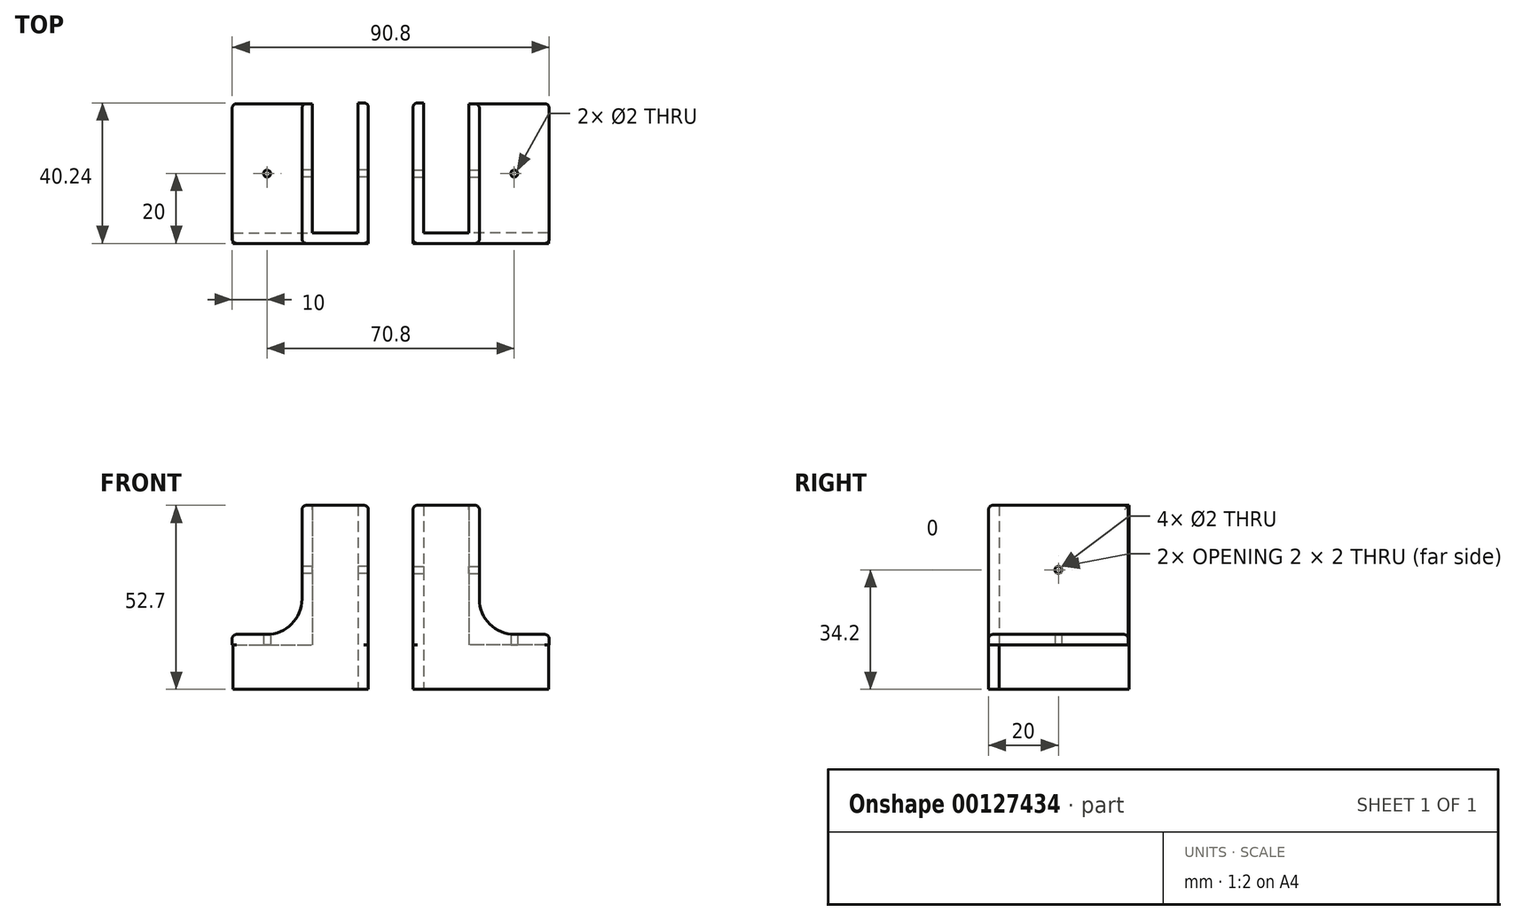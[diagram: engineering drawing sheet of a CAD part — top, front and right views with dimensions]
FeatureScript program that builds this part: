
annotation { "Feature Type Name" : "Feature", "Feature Type Description" : "" }
export const myFeature = defineFeature(function(context is Context, id is Id, definition is map)
    precondition{}
    {
        {
            var Q0;
            Q0=qCreatedBy(makeId("Top.planeOp"),FACE);
            var sketch = newSketch(context, id + "F0", { "sketchPlane" : qUnion([Q0])});
            skLineSegment(sketch, "E0.bottom", {"start": v(0, 0) * mm, "end": v(-20, 0) * mm});
            skLineSegment(sketch, "E0.top", {"start": v(0, 40) * mm, "end": v(-20, 40) * mm});
            skLineSegment(sketch, "E0.left", {"start": v(0, 0) * mm, "end": v(0, 40) * mm});
            skLineSegment(sketch, "E0.right", {"start": v(-20, 0) * mm, "end": v(-20, 40) * mm});
            skLineSegment(sketch, "E1", {"start": v(0, 40) * mm, "end": v(3, 40) * mm});
            skLineSegment(sketch, "E2", {"start": v(3, 40) * mm, "end": v(3, 3) * mm});
            skLineSegment(sketch, "E3", {"start": v(3, 3) * mm, "end": v(16, 3) * mm});
            skLineSegment(sketch, "E4", {"start": v(16, 3) * mm, "end": v(16, 40.24) * mm});
            skLineSegment(sketch, "E5", {"start": v(16, 40.24) * mm, "end": v(19, 40.24) * mm});
            skLineSegment(sketch, "E6", {"start": v(19, 40.24) * mm, "end": v(19, 0) * mm});
            skLineSegment(sketch, "E7", {"start": v(19, 0) * mm, "end": v(0, 0) * mm});
            skLineSegment(sketch, "E8", {"start": v(0, 20) * mm, "end": v(54.2, 20) * mm, "construction": true});
            skLineSegment(sketch, "E9", {"start": v(54.2, 20) * mm, "end": v(-70.8, 20) * mm, "construction": true});
            skCircle(sketch, "E10", {"center": v(-10, 20) * mm, "radius": 1 * mm});
            skPoint(sketch, "E10.centerSnap0", {"position": v(-10, 40) * mm});
            skPoint(sketch, "E10.centerSnap1", {"position": v(-8.3, 20) * mm});
            skLineSegment(sketch, "E11", {"start": v(3, 3) * mm, "end": v(3, 0) * mm});
            skSolve(sketch);
        }
        {
            var Q0;
            Q0=makeQuery(id+"F0.imprint","IMPRINT",FACE,{"disambiguationData":[TD([[makeQuery(id+"F0.imprint","IMPRINT",EDGE,{"derivedFrom":sQuery(id+"F0.wireOp",EDGE,"E0.left")}),-1.0]])]});
            var Q1;
            Q1=makeQuery(id+"F0.imprint","IMPRINT",FACE,{"disambiguationData":[TD([[makeQuery(id+"F0.imprint","IMPRINT",EDGE,{"derivedFrom":sQuery(id+"F0.wireOp",EDGE,"E3")}),-1.0]])]});
            extrude(context, id + "F1", {"entities" : qUnion([Q0, Q1]), "depth" : 40 * mm});
        }
        {
            var Q0;
            Q0 = qSketchRegion(id + "F0", true);
            extrude(context, id + "F2", {"entities" : qUnion([Q0]), "operationType" : NewBodyOperationType.ADD, "depth" : 3 * mm});
        }
        {
            var Q0;
            Q0=makeQuery(id+"F1.opExtrude","SWEPT_FACE",FACE,{"disambiguationData":[OSD([sQuery(id+"F0.wireOp",EDGE,"E0.left")])]});
            var sketch = newSketch(context, id + "F3", { "sketchPlane" : qUnion([Q0])});
            skCircle(sketch, "E12", {"center": v(-20, 21.5) * mm, "radius": 1 * mm});
            skPoint(sketch, "E12.centerSnap0", {"position": v(-20, 40) * mm});
            skPoint(sketch, "E12.centerSnap1", {"position": v(0, 21.5) * mm});
            skSolve(sketch);
        }
        {
            var Q0;
            Q0=makeQuery(id+"F3.imprint","IMPRINT",FACE,{"disambiguationData":[TD([[makeQuery(id+"F3.imprint","IMPRINT",EDGE,{"derivedFrom":sQuery(id+"F3.wireOp",EDGE,"E12")}),1.0]])]});
            extrude(context, id + "F4", {"entities" : qUnion([Q0]), "operationType" : NewBodyOperationType.REMOVE, "oppositeDirection" : true, "depth" : 25.4 * mm});
        }
        {
            var Q0;
            Q0=makeQuery(id+"F2.opExtrude","CAP_EDGE",EDGE,{"disambiguationData":[OSD([sQuery(id+"F0.wireOp",EDGE,"E0.right")])],"isStart":false});
            var Q1;
            Q1=makeQuery(id+"F1.opExtrude","CAP_EDGE",EDGE,{"disambiguationData":[OSD([sQuery(id+"F0.wireOp",EDGE,"E0.left")])],"isStart":false});
            var Q2;
            Q2=makeQuery(id+"F1.opExtrude","SWEPT_EDGE",EDGE,{"disambiguationData":[OSD([sQuery(id+"F0.wireOp",EDGE,"E5"),sQuery(id+"F0.wireOp",EDGE,"E6")])]});
            var Q3;
            Q3=makeQuery(id+"F1.opExtrude","CAP_EDGE",EDGE,{"disambiguationData":[OSD([sQuery(id+"F0.wireOp",EDGE,"E6")])],"isStart":false});
            var Q4;
            Q4=makeQuery(id+"F1.opExtrude","CAP_EDGE",EDGE,{"disambiguationData":[OSD([sQuery(id+"F0.wireOp",EDGE,"E7")])],"isStart":false});
            var Q5;
            Q5=makeQuery(id+"F1.opExtrude","SWEPT_EDGE",EDGE,{"disambiguationData":[OSD([sQuery(id+"F0.wireOp",EDGE,"E6"),sQuery(id+"F0.wireOp",EDGE,"E7")])]});
            fillet(context, id + "F5", {"entities" : qUnion([Q0, Q1, Q2, Q3, Q4, Q5]), "radius" : 1.27 * mm, "tangentPropagation" : true, "allowEdgeOverflow" : false});
        }
        {
            var Q0;
            Q0=makeQuery(id+"F2.boolean.opBoolean","INTERSECT",EDGE,{"derivedFrom":[makeQuery(id+"F1.opExtrude","SWEPT_FACE",FACE,{"disambiguationData":[OSD([sQuery(id+"F0.wireOp",EDGE,"E0.left")])]}),makeQuery(id+"F2.opExtrude","CAP_FACE",FACE,{"disambiguationData":[OSD([sQuery(id+"F0.wireOp",EDGE,"E0.bottom"),sQuery(id+"F0.wireOp",EDGE,"E0.top"),sQuery(id+"F0.wireOp",EDGE,"E0.right"),sQuery(id+"F0.wireOp",EDGE,"E1"),sQuery(id+"F0.wireOp",EDGE,"E2"),sQuery(id+"F0.wireOp",EDGE,"E3"),sQuery(id+"F0.wireOp",EDGE,"E4"),sQuery(id+"F0.wireOp",EDGE,"E5"),sQuery(id+"F0.wireOp",EDGE,"E6"),sQuery(id+"F0.wireOp",EDGE,"E7"),sQuery(id+"F0.wireOp",EDGE,"E10")])],"isStart":false})]});
            fillet(context, id + "F6", {"entities" : qUnion([Q0]), "radius" : 10.16 * mm, "tangentPropagation" : true, "allowEdgeOverflow" : false});
        }
        {
            var Q0;
            Q0=makeQuery(id+"F1.opExtrude","SWEPT_EDGE",EDGE,{"disambiguationData":[OSD([sQuery(id+"F0.wireOp",EDGE,"E0.top"),sQuery(id+"F0.wireOp",EDGE,"E0.left"),sQuery(id+"F0.wireOp",EDGE,"E1")])]});
            var Q1;
            Q1=makeQuery(id+"F1.opExtrude","SWEPT_EDGE",EDGE,{"disambiguationData":[OSD([sQuery(id+"F0.wireOp",EDGE,"E0.bottom"),sQuery(id+"F0.wireOp",EDGE,"E0.left"),sQuery(id+"F0.wireOp",EDGE,"E7")])]});
            fillet(context, id + "F7", {"entities" : qUnion([Q0, Q1]), "radius" : 1.27 * mm, "tangentPropagation" : true, "allowEdgeOverflow" : false});
        }
        {
            var Q0;
            Q0=qCreatedBy(makeId("Right.planeOp"),FACE);
            cPlane(context, id + "F8", {"entities" : qUnion([Q0]), "cplaneType" : CPlaneType.OFFSET, "offset" : 25.4 * mm, "width" : 152.4 * mm, "height" : 152.4 * mm});
        }
        {
            var Q0;
            Q0=makeQuery(id+"F0.imprint","IMPRINT",FACE,{"disambiguationData":[TD([[makeQuery(id+"F0.imprint","IMPRINT",EDGE,{"derivedFrom":sQuery(id+"F0.wireOp",EDGE,"E3")}),-1.0]])]});
            extrude(context, id + "F9", {"entities" : qUnion([Q0]), "operationType" : NewBodyOperationType.ADD, "oppositeDirection" : true, "depth" : 12.7 * mm});
        }
        {
            var Q0;
            Q0=makeQuery(id+"F9.opExtrude","SWEPT_FACE",FACE,{"disambiguationData":[OSD([sQuery(id+"F0.wireOp",EDGE,"E11")])]});
            extrude(context, id + "F10", {"entities" : qUnion([Q0]), "operationType" : NewBodyOperationType.ADD, "depth" : 22.82 * mm});
        }
        {
            var Q0;
            Q0=makeQuery(id+"F9.opExtrude","SWEPT_EDGE",EDGE,{"disambiguationData":[OSD([sQuery(id+"F0.wireOp",EDGE,"E5"),sQuery(id+"F0.wireOp",EDGE,"E6")])]});
            fillet(context, id + "F11", {"entities" : qUnion([Q0]), "radius" : 1.27 * mm, "tangentPropagation" : true, "allowEdgeOverflow" : false});
        }
        {
            var Q0;
            Q0=makeQuery(id+"F1.opExtrude","SWEPT_BODY",BODY,{"disambiguationData":[OSD([sQuery(id+"F0.wireOp",EDGE,"E0.left"),sQuery(id+"F0.wireOp",EDGE,"E1"),sQuery(id+"F0.wireOp",EDGE,"E2"),sQuery(id+"F0.wireOp",EDGE,"E3"),sQuery(id+"F0.wireOp",EDGE,"E4"),sQuery(id+"F0.wireOp",EDGE,"E5"),sQuery(id+"F0.wireOp",EDGE,"E6"),sQuery(id+"F0.wireOp",EDGE,"E7")])]});
            var Q1;
            Q1=qCreatedBy(id+"F8.planeOp",FACE);
            mirror(context, id + "F12", {"entities" : qUnion([Q0]), "mirrorPlane" : qUnion([Q1])});
        }
    });
